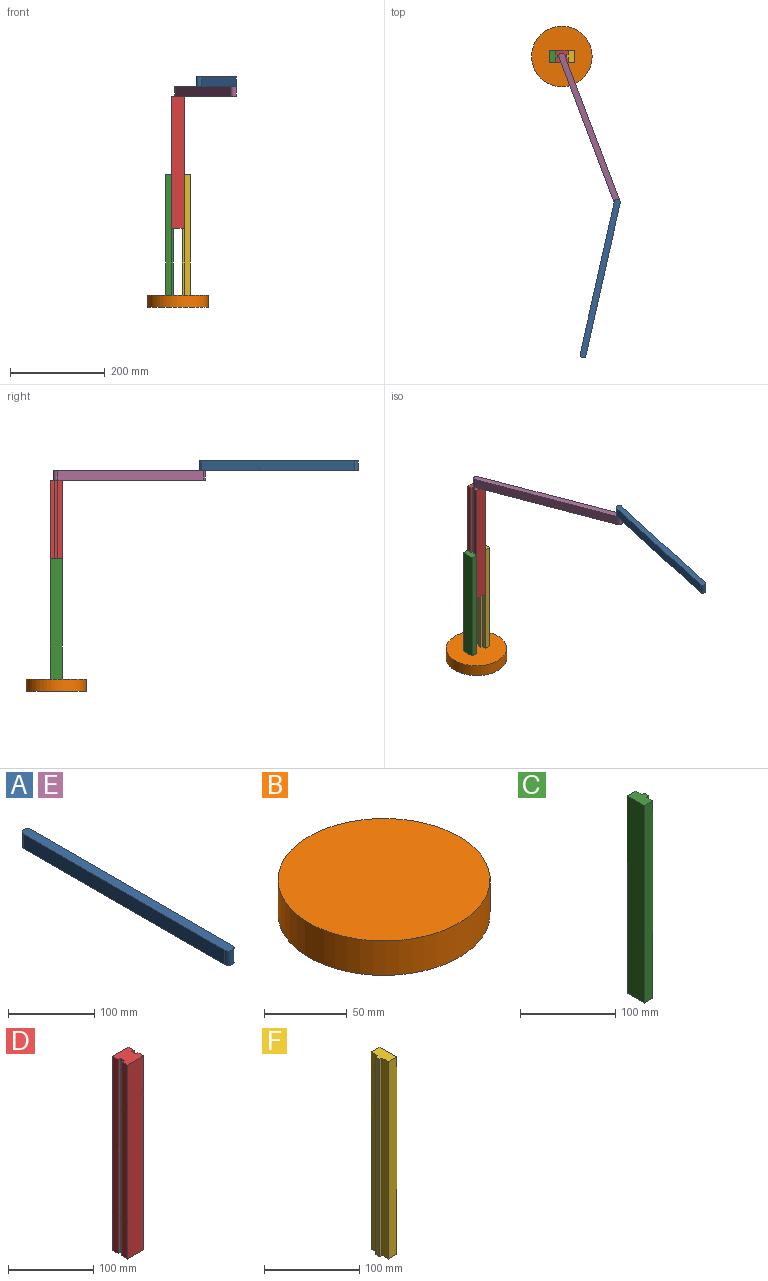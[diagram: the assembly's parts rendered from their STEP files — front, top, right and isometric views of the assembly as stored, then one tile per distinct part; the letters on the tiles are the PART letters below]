
ASSEMBLY  parts=6 mates=5
PART A: 6 faces, bbox 12.7x342.9x20.3 mm
  f0: cylinder r=6.35mm len=20.32mm, axis (0,0,-1), area 405.4mm2, adj f1,f3,f4,f5
  f1: plane 330.2x20.32mm, normal (-1,0,0), area 6709.7mm2, adj f0,f2,f4,f5
  f2: cylinder r=6.35mm len=20.32mm, axis (0,0,-1), area 405.4mm2, adj f1,f3,f4,f5
  f3: plane 330.2x20.32mm, normal (1,0,0), area 6709.7mm2, adj f0,f2,f4,f5
  f4: plane 342.9x12.7mm, normal (0,0,1), area 4320.2mm2, adj f0,f1,f2,f3
  f5: plane 342.9x12.7mm, normal (0,0,-1), area 4320.2mm2, adj f0,f1,f2,f3
PART B: 3 faces, bbox 127.8x127.8x25.4 mm
  f0: cylinder r=63.9mm len=127.8mm, axis (0,0,-1), area 10197.8mm2, adj f1,f2
  f1: plane 127.8x127.8mm, normal (0,0,1), area 12827.4mm2, adj f0
  f2: plane 127.8x127.8mm, normal (0,0,-1), area 12827.4mm2, adj f0
PART C: 10 faces, bbox 16.5x25.4x254 mm
  f0: plane 254x3.81mm, normal (0,-1,0), area 967.7mm2, adj f1,f7,f8,f9
  f1: plane 254x6.35mm, normal (1,0,0), area 1612.9mm2, adj f0,f2,f8,f9
  f2: plane 254x3.81mm, normal (0,1,0), area 967.7mm2, adj f1,f3,f8,f9
  f3: plane 254x9.53mm, normal (1,0,0), area 2419.3mm2, adj f2,f4,f8,f9
  f4: plane 254x12.7mm, normal (0,1,0), area 3225.8mm2, adj f3,f5,f8,f9
  f5: plane 254x25.4mm, normal (-1,0,0), area 6451.6mm2, adj f4,f6,f8,f9
  f6: plane 254x12.7mm, normal (0,-1,0), area 3225.8mm2, adj f5,f7,f8,f9
  f7: plane 254x9.53mm, normal (1,0,0), area 2419.3mm2, adj f0,f6,f8,f9
  f8: plane 25.4x16.51mm, normal (0,0,1), area 346.8mm2, adj f0,f1,f2,f3,f4,f5,f6,f7
  f9: plane 25.4x16.51mm, normal (0,0,-1), area 346.8mm2, adj f0,f1,f2,f3,f4,f5,f6,f7
PART D: 14 faces, bbox 26.7x25.4x279.4 mm
  f0: plane 279.4x3.81mm, normal (0,-1,0), area 1064.5mm2, adj f1,f11,f12,f13
  f1: plane 279.4x6.35mm, normal (-1,0,0), area 1774.2mm2, adj f0,f2,f12,f13
  f2: plane 279.4x3.81mm, normal (0,1,0), area 1064.5mm2, adj f1,f3,f12,f13
  f3: plane 279.4x9.53mm, normal (-1,0,0), area 2661.3mm2, adj f2,f4,f12,f13
  f4: plane 279.4x26.67mm, normal (0,-1,0), area 7451.6mm2, adj f3,f5,f12,f13
  f5: plane 279.4x9.53mm, normal (1,0,0), area 2661.3mm2, adj f4,f6,f12,f13
  f6: plane 279.4x3.81mm, normal (0,1,0), area 1064.5mm2, adj f5,f7,f12,f13
  f7: plane 279.4x6.35mm, normal (1,0,0), area 1774.2mm2, adj f6,f8,f12,f13
  f8: plane 279.4x3.81mm, normal (0,-1,0), area 1064.5mm2, adj f7,f9,f12,f13
  f9: plane 279.4x9.53mm, normal (1,0,0), area 2661.3mm2, adj f8,f10,f12,f13
  f10: plane 279.4x26.67mm, normal (0,1,0), area 7451.6mm2, adj f9,f11,f12,f13
  f11: plane 279.4x9.53mm, normal (-1,0,0), area 2661.3mm2, adj f0,f10,f12,f13
  f12: plane 26.67x25.4mm, normal (0,0,1), area 629mm2, adj f0,f1,f2,f3,f4,f5,f6,f7
  f13: plane 26.67x25.4mm, normal (0,0,-1), area 629mm2, adj f0,f1,f2,f3,f4,f5,f6,f7
PART E: same geometry as A
PART F: 10 faces, bbox 16.5x25.4x254 mm
  f0: plane 254x3.81mm, normal (0,-1,0), area 967.7mm2, adj f1,f7,f8,f9
  f1: plane 254x9.53mm, normal (-1,0,0), area 2419.3mm2, adj f0,f2,f8,f9
  f2: plane 254x12.7mm, normal (0,-1,0), area 3225.8mm2, adj f1,f3,f8,f9
  f3: plane 254x25.4mm, normal (1,0,0), area 6451.6mm2, adj f2,f4,f8,f9
  f4: plane 254x12.7mm, normal (0,1,0), area 3225.8mm2, adj f3,f5,f8,f9
  f5: plane 254x9.53mm, normal (-1,0,0), area 2419.3mm2, adj f4,f6,f8,f9
  f6: plane 254x3.81mm, normal (0,1,0), area 967.7mm2, adj f5,f7,f8,f9
  f7: plane 254x6.35mm, normal (-1,0,0), area 1612.9mm2, adj f0,f6,f8,f9
  f8: plane 25.4x16.51mm, normal (0,0,1), area 346.8mm2, adj f0,f1,f2,f3,f4,f5,f6,f7
  f9: plane 25.4x16.51mm, normal (0,0,-1), area 346.8mm2, adj f0,f1,f2,f3,f4,f5,f6,f7
PLACE A rot(axis=(0,0,-1),12.7deg) t=(57.23,-575.34,465.81)mm
PLACE B at identity fixed
PLACE C t=(0.06,0,25.4)mm
PLACE D t=(0,0,166.09)mm
PLACE E rot(axis=(0,0,1),20.8deg) t=(97.01,-255.5,445.49)mm
PLACE F t=(-0.06,0,25.4)mm
MATE fastened F.f9 <-> B.f1  axis (0,0,-1) through (19.05,0,25.4)mm
MATE revolute E.f2 <-> A.f0  axis (0,0,1) through (117.21,-308.7,465.81)mm
MATE slider F.f8 <-> D.f12  axis (0,0,1) through (19.05,0,279.4)mm
MATE revolute E.f0 <-> D.f12  axis (0,0,-1) through (0,0,445.49)mm
MATE fastened C.f9 <-> B.f1  axis (0,0,-1) through (-19.05,0,25.4)mm
